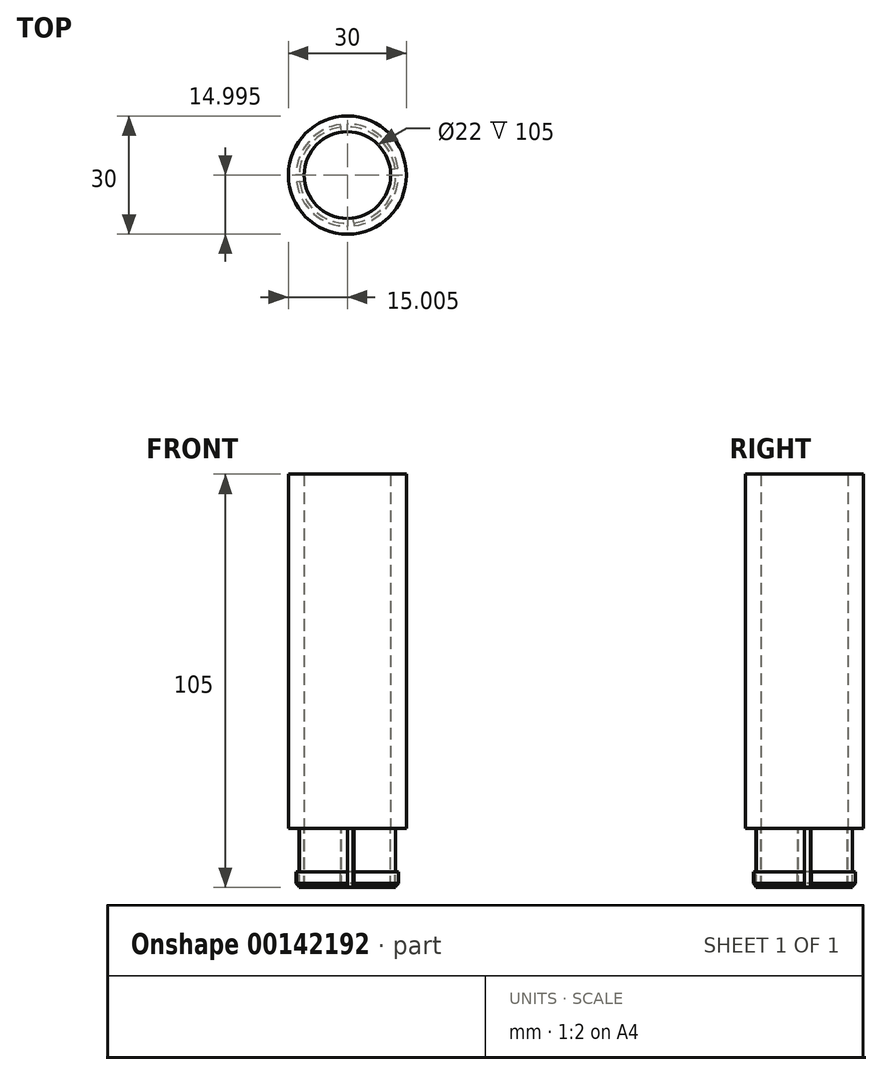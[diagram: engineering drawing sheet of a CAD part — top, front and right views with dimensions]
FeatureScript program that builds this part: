
annotation { "Feature Type Name" : "Feature", "Feature Type Description" : "" }
export const myFeature = defineFeature(function(context is Context, id is Id, definition is map)
    precondition{}
    {
        {
            var Q0;
            Q0=qCreatedBy(makeId("Top.planeOp"),FACE);
            var sketch = newSketch(context, id + "F0", { "sketchPlane" : qUnion([Q0])});
            skCircle(sketch, "E0", {"center": v(-39.95, 28.1) * mm, "radius": 15 * mm});
            skCircle(sketch, "E1", {"center": v(-39.95, 28.1) * mm, "radius": 12.25 * mm});
            skCircle(sketch, "E2", {"center": v(-39.95, 28.1) * mm, "radius": 11 * mm});
            skLineSegment(sketch, "E3", {"start": v(-39.95, 17.1) * mm, "end": v(-39.95, 15.86) * mm});
            skLineSegment(sketch, "E4", {"start": v(-39.95, 15.86) * mm, "end": v(-39.95, 17.1) * mm});
            skLineSegment(sketch, "E5", {"start": v(-39.95, 39.1) * mm, "end": v(-39.95, 40.36) * mm});
            skLineSegment(sketch, "E6", {"start": v(-39.95, 40.36) * mm, "end": v(-39.95, 39.1) * mm});
            skLineSegment(sketch, "E7", {"start": v(-28.95, 28.1) * mm, "end": v(-27.7, 28.1) * mm});
            skLineSegment(sketch, "E8", {"start": v(-27.7, 28.1) * mm, "end": v(-28.95, 28.1) * mm});
            skLineSegment(sketch, "E9", {"start": v(-50.95, 28.1) * mm, "end": v(-52.2, 28.1) * mm});
            skLineSegment(sketch, "E10", {"start": v(-52.2, 28.1) * mm, "end": v(-50.95, 28.1) * mm});
            skLineSegment(sketch, "E11", {"start": v(-29.04, 29.57) * mm, "end": v(-27.8, 29.74) * mm});
            skLineSegment(sketch, "E12", {"start": v(-27.8, 29.74) * mm, "end": v(-29.04, 29.57) * mm});
            skLineSegment(sketch, "E13", {"start": v(-52.09, 26.47) * mm, "end": v(-50.85, 26.64) * mm});
            skLineSegment(sketch, "E14", {"start": v(-41.41, 39) * mm, "end": v(-41.58, 40.25) * mm});
            skLineSegment(sketch, "E15", {"start": v(-41.58, 40.25) * mm, "end": v(-41.41, 39) * mm});
            skLineSegment(sketch, "E16", {"start": v(-38.3, 15.96) * mm, "end": v(-38.48, 17.2) * mm});
            skLineSegment(sketch, "E17.trimOffspring", {"start": v(-38.48, 17.2) * mm, "end": v(-38.3, 15.96) * mm});
            skLineSegment(sketch, "E18.trimOffspring", {"start": v(-50.85, 26.64) * mm, "end": v(-52.09, 26.47) * mm});
            skCircle(sketch, "E19", {"center": v(-39.95, 28.1) * mm, "radius": 13 * mm});
            skLineSegment(sketch, "E20", {"start": v(-50.95, 28.1) * mm, "end": v(-52.95, 28.1) * mm});
            skLineSegment(sketch, "E21", {"start": v(-50.85, 26.64) * mm, "end": v(-52.83, 26.37) * mm});
            skLineSegment(sketch, "E22", {"start": v(-41.41, 39) * mm, "end": v(-41.68, 40.99) * mm});
            skLineSegment(sketch, "E23", {"start": v(-39.95, 39.1) * mm, "end": v(-39.95, 41.1) * mm});
            skLineSegment(sketch, "E24", {"start": v(-29.04, 29.57) * mm, "end": v(-27.06, 29.84) * mm});
            skLineSegment(sketch, "E25", {"start": v(-28.95, 28.1) * mm, "end": v(-26.95, 28.1) * mm});
            skLineSegment(sketch, "E26", {"start": v(-39.95, 17.1) * mm, "end": v(-39.95, 15.1) * mm});
            skLineSegment(sketch, "E27", {"start": v(-38.48, 17.2) * mm, "end": v(-38.2, 15.22) * mm});
            skSolve(sketch);
        }
        {
            var Q0;
            Q0 = qSketchRegion(id + "F0", true);
            var Q1;
            {var subQ0=sQuery(id+"F0.wireOp",EDGE,"E4");Q1=makeQuery(id+"F0.imprint","IMPRINT",FACE,{"disambiguationData":[TD([[makeQuery(id+"F0.imprint","IMPRINT",EDGE,{"derivedFrom":subQ0}),1.0]])]});}
            var Q2;
            Q2=makeQuery(id+"F0.imprint","IMPRINT",FACE,{"disambiguationData":[TD([[makeQuery(id+"F0.imprint","IMPRINT",EDGE,{"derivedFrom":sQuery(id+"F0.wireOp",EDGE,"E19")}),1.0]])]});
            var Q3;
            {var subQ0=sQuery(id+"F0.wireOp",EDGE,"E8");Q3=makeQuery(id+"F0.imprint","IMPRINT",FACE,{"disambiguationData":[TD([[makeQuery(id+"F0.imprint","IMPRINT",EDGE,{"derivedFrom":subQ0}),1.0]])]});}
            var Q4;
            {var subQ0=sQuery(id+"F0.wireOp",EDGE,"E6");Q4=makeQuery(id+"F0.imprint","IMPRINT",FACE,{"disambiguationData":[TD([[makeQuery(id+"F0.imprint","IMPRINT",EDGE,{"derivedFrom":subQ0}),1.0]])]});}
            var Q5;
            {var subQ0=sQuery(id+"F0.wireOp",EDGE,"E10");Q5=makeQuery(id+"F0.imprint","IMPRINT",FACE,{"disambiguationData":[TD([[makeQuery(id+"F0.imprint","IMPRINT",EDGE,{"derivedFrom":subQ0}),1.0]])]});}
            var Q6;
            {var subQ0=sQuery(id+"F0.wireOp",EDGE,"E6");Q6=makeQuery(id+"F0.imprint","IMPRINT",FACE,{"disambiguationData":[TD([[makeQuery(id+"F0.imprint","IMPRINT",EDGE,{"derivedFrom":subQ0}),-1.0]])]});}
            var Q7;
            {var subQ0=sQuery(id+"F0.wireOp",EDGE,"E8");Q7=makeQuery(id+"F0.imprint","IMPRINT",FACE,{"disambiguationData":[TD([[makeQuery(id+"F0.imprint","IMPRINT",EDGE,{"derivedFrom":subQ0}),-1.0]])]});}
            var Q8;
            {var subQ0=sQuery(id+"F0.wireOp",EDGE,"E4");Q8=makeQuery(id+"F0.imprint","IMPRINT",FACE,{"disambiguationData":[TD([[makeQuery(id+"F0.imprint","IMPRINT",EDGE,{"derivedFrom":subQ0}),-1.0]])]});}
            var Q9;
            {var subQ0=sQuery(id+"F0.wireOp",EDGE,"E10");Q9=makeQuery(id+"F0.imprint","IMPRINT",FACE,{"disambiguationData":[TD([[makeQuery(id+"F0.imprint","IMPRINT",EDGE,{"derivedFrom":subQ0}),-1.0]])]});}
            var Q10;
            {var subQ0=sQuery(id+"F0.wireOp",EDGE,"E22");var subQ1=sQuery(id+"F0.wireOp",EDGE,"E1");var subQ2=makeQuery(id+"F0.imprint","INTERSECT",VERTEX,{"derivedFrom":[subQ1,subQ0]});Q10=makeQuery(id+"F0.imprint","IMPRINT",FACE,{"disambiguationData":[TD([[makeQuery(id+"F0.imprint","IMPRINT",EDGE,{"disambiguationData":[TD([[subQ2,-1.0]])],"derivedFrom":subQ1}),1.0]])]});}
            var Q11;
            {var subQ0=sQuery(id+"F0.wireOp",EDGE,"E23");var subQ1=sQuery(id+"F0.wireOp",EDGE,"E1");var subQ2=makeQuery(id+"F0.imprint","INTERSECT",VERTEX,{"derivedFrom":[subQ1,subQ0]});Q11=makeQuery(id+"F0.imprint","IMPRINT",FACE,{"disambiguationData":[TD([[makeQuery(id+"F0.imprint","IMPRINT",EDGE,{"disambiguationData":[TD([[subQ2,-1.0]])],"derivedFrom":subQ1}),1.0]])]});}
            var Q12;
            {var subQ0=sQuery(id+"F0.wireOp",EDGE,"E24");var subQ1=sQuery(id+"F0.wireOp",EDGE,"E1");var subQ2=makeQuery(id+"F0.imprint","INTERSECT",VERTEX,{"derivedFrom":[subQ1,subQ0]});Q12=makeQuery(id+"F0.imprint","IMPRINT",FACE,{"disambiguationData":[TD([[makeQuery(id+"F0.imprint","IMPRINT",EDGE,{"disambiguationData":[TD([[subQ2,-1.0]])],"derivedFrom":subQ1}),1.0]])]});}
            var Q13;
            {var subQ0=sQuery(id+"F0.wireOp",EDGE,"E24");var subQ1=sQuery(id+"F0.wireOp",EDGE,"E1");var subQ2=makeQuery(id+"F0.imprint","INTERSECT",VERTEX,{"derivedFrom":[subQ1,subQ0]});Q13=makeQuery(id+"F0.imprint","IMPRINT",FACE,{"disambiguationData":[TD([[makeQuery(id+"F0.imprint","IMPRINT",EDGE,{"disambiguationData":[TD([[subQ2,1.0]])],"derivedFrom":subQ1}),1.0]])]});}
            var Q14;
            {var subQ0=sQuery(id+"F0.wireOp",EDGE,"E25");var subQ1=sQuery(id+"F0.wireOp",EDGE,"E1");var subQ2=makeQuery(id+"F0.imprint","INTERSECT",VERTEX,{"derivedFrom":[subQ1,subQ0]});Q14=makeQuery(id+"F0.imprint","IMPRINT",FACE,{"disambiguationData":[TD([[makeQuery(id+"F0.imprint","IMPRINT",EDGE,{"disambiguationData":[TD([[subQ2,1.0]])],"derivedFrom":subQ1}),1.0]])]});}
            var Q15;
            {var subQ0=sQuery(id+"F0.wireOp",EDGE,"E26");var subQ1=sQuery(id+"F0.wireOp",EDGE,"E1");var subQ2=makeQuery(id+"F0.imprint","INTERSECT",VERTEX,{"derivedFrom":[subQ1,subQ0]});Q15=makeQuery(id+"F0.imprint","IMPRINT",FACE,{"disambiguationData":[TD([[makeQuery(id+"F0.imprint","IMPRINT",EDGE,{"disambiguationData":[TD([[subQ2,-1.0]])],"derivedFrom":subQ1}),1.0]])]});}
            var Q16;
            {var subQ0=sQuery(id+"F0.wireOp",EDGE,"E21");var subQ1=sQuery(id+"F0.wireOp",EDGE,"E1");var subQ2=makeQuery(id+"F0.imprint","INTERSECT",VERTEX,{"derivedFrom":[subQ1,subQ0]});Q16=makeQuery(id+"F0.imprint","IMPRINT",FACE,{"disambiguationData":[TD([[makeQuery(id+"F0.imprint","IMPRINT",EDGE,{"disambiguationData":[TD([[subQ2,-1.0]])],"derivedFrom":subQ1}),1.0]])]});}
            var Q17;
            {var subQ0=sQuery(id+"F0.wireOp",EDGE,"E20");var subQ1=sQuery(id+"F0.wireOp",EDGE,"E1");var subQ2=makeQuery(id+"F0.imprint","INTERSECT",VERTEX,{"derivedFrom":[subQ1,subQ0]});Q17=makeQuery(id+"F0.imprint","IMPRINT",FACE,{"disambiguationData":[TD([[makeQuery(id+"F0.imprint","IMPRINT",EDGE,{"disambiguationData":[TD([[subQ2,-1.0]])],"derivedFrom":subQ1}),1.0]])]});}
            extrude(context, id + "F1", {"entities" : qUnion([Q0, Q1, Q2, Q3, Q4, Q5, Q6, Q7, Q8, Q9, Q10, Q11, Q12, Q13, Q14, Q15, Q16, Q17]), "depth" : 90 * mm});
        }
        {
            var Q0;
            {var subQ0=sQuery(id+"F0.wireOp",EDGE,"E22");var subQ1=sQuery(id+"F0.wireOp",EDGE,"E1");var subQ2=makeQuery(id+"F0.imprint","INTERSECT",VERTEX,{"derivedFrom":[subQ1,subQ0]});Q0=makeQuery(id+"F0.imprint","IMPRINT",FACE,{"disambiguationData":[TD([[makeQuery(id+"F0.imprint","IMPRINT",EDGE,{"disambiguationData":[TD([[subQ2,-1.0]])],"derivedFrom":subQ1}),1.0]])]});}
            var Q1;
            {var subQ0=sQuery(id+"F0.wireOp",EDGE,"E24");var subQ1=sQuery(id+"F0.wireOp",EDGE,"E1");var subQ2=makeQuery(id+"F0.imprint","INTERSECT",VERTEX,{"derivedFrom":[subQ1,subQ0]});Q1=makeQuery(id+"F0.imprint","IMPRINT",FACE,{"disambiguationData":[TD([[makeQuery(id+"F0.imprint","IMPRINT",EDGE,{"disambiguationData":[TD([[subQ2,-1.0]])],"derivedFrom":subQ1}),1.0]])]});}
            var Q2;
            {var subQ0=sQuery(id+"F0.wireOp",EDGE,"E25");var subQ1=sQuery(id+"F0.wireOp",EDGE,"E1");var subQ2=makeQuery(id+"F0.imprint","INTERSECT",VERTEX,{"derivedFrom":[subQ1,subQ0]});Q2=makeQuery(id+"F0.imprint","IMPRINT",FACE,{"disambiguationData":[TD([[makeQuery(id+"F0.imprint","IMPRINT",EDGE,{"disambiguationData":[TD([[subQ2,1.0]])],"derivedFrom":subQ1}),1.0]])]});}
            var Q3;
            {var subQ0=sQuery(id+"F0.wireOp",EDGE,"E21");var subQ1=sQuery(id+"F0.wireOp",EDGE,"E1");var subQ2=makeQuery(id+"F0.imprint","INTERSECT",VERTEX,{"derivedFrom":[subQ1,subQ0]});Q3=makeQuery(id+"F0.imprint","IMPRINT",FACE,{"disambiguationData":[TD([[makeQuery(id+"F0.imprint","IMPRINT",EDGE,{"disambiguationData":[TD([[subQ2,-1.0]])],"derivedFrom":subQ1}),1.0]])]});}
            extrude(context, id + "F2", {"entities" : qUnion([Q0, Q1, Q2, Q3]), "operationType" : NewBodyOperationType.ADD, "oppositeDirection" : true, "depth" : 15 * mm});
        }
        {
            var Q0;
            {var subQ0=sQuery(id+"F0.wireOp",EDGE,"E24");var subQ1=sQuery(id+"F0.wireOp",EDGE,"E1");var subQ2=makeQuery(id+"F0.imprint","INTERSECT",VERTEX,{"derivedFrom":[subQ1,subQ0]});Q0=makeQuery(id+"F0.imprint","IMPRINT",FACE,{"disambiguationData":[TD([[makeQuery(id+"F0.imprint","IMPRINT",EDGE,{"disambiguationData":[TD([[subQ2,-1.0]])],"derivedFrom":subQ1}),-1.0]])]});}
            var Q1;
            {var subQ0=sQuery(id+"F0.wireOp",EDGE,"E21");var subQ1=sQuery(id+"F0.wireOp",EDGE,"E1");var subQ2=makeQuery(id+"F0.imprint","INTERSECT",VERTEX,{"derivedFrom":[subQ1,subQ0]});Q1=makeQuery(id+"F0.imprint","IMPRINT",FACE,{"disambiguationData":[TD([[makeQuery(id+"F0.imprint","IMPRINT",EDGE,{"disambiguationData":[TD([[subQ2,-1.0]])],"derivedFrom":subQ1}),-1.0]])]});}
            var Q2;
            {var subQ0=sQuery(id+"F0.wireOp",EDGE,"E25");var subQ1=sQuery(id+"F0.wireOp",EDGE,"E1");var subQ2=makeQuery(id+"F0.imprint","INTERSECT",VERTEX,{"derivedFrom":[subQ1,subQ0]});Q2=makeQuery(id+"F0.imprint","IMPRINT",FACE,{"disambiguationData":[TD([[makeQuery(id+"F0.imprint","IMPRINT",EDGE,{"disambiguationData":[TD([[subQ2,1.0]])],"derivedFrom":subQ1}),-1.0]])]});}
            var Q3;
            {var subQ0=sQuery(id+"F0.wireOp",EDGE,"E22");var subQ1=sQuery(id+"F0.wireOp",EDGE,"E1");var subQ2=makeQuery(id+"F0.imprint","INTERSECT",VERTEX,{"derivedFrom":[subQ1,subQ0]});Q3=makeQuery(id+"F0.imprint","IMPRINT",FACE,{"disambiguationData":[TD([[makeQuery(id+"F0.imprint","IMPRINT",EDGE,{"disambiguationData":[TD([[subQ2,-1.0]])],"derivedFrom":subQ1}),-1.0]])]});}
            var Q4;
            Q4=makeQuery(id+"F2.opExtrude","CAP_FACE",FACE,{"disambiguationData":[OSD([sQuery(id+"F0.wireOp",EDGE,"E1"),sQuery(id+"F0.wireOp",EDGE,"E2"),sQuery(id+"F0.wireOp",EDGE,"E25"),sQuery(id+"F0.wireOp",EDGE,"E27")])],"isStart":false});
            extrude(context, id + "F3", {"entities" : qUnion([Q0, Q1, Q2, Q3]), "endBound" : BoundingType.UP_TO_SURFACE, "oppositeDirection" : true, "endBoundEntityFace" : qUnion([Q4]), "depth" : 25 * mm, "hasSecondDirection" : true, "secondDirectionOppositeDirection" : true, "secondDirectionDepth" : 11 * mm});
        }
        {
            var Q0;
            {var subQ0=sQuery(id+"F0.wireOp",EDGE,"E19");Q0=makeQuery(id+"F3.opExtrude","CAP_EDGE",EDGE,{"disambiguationData":[OSD([subQ0]),TDD([makeQuery(id+"F0.imprint","IMPRINT",EDGE,{"disambiguationData":[TD([[makeQuery(id+"F0.imprint","INTERSECT",VERTEX,{"derivedFrom":[subQ0,sQuery(id+"F0.wireOp",EDGE,"E25")]}),1.0]])],"derivedFrom":subQ0})])],"isStart":false});}
            var Q1;
            {var subQ0=sQuery(id+"F0.wireOp",EDGE,"E19");Q1=makeQuery(id+"F3.opExtrude","CAP_EDGE",EDGE,{"disambiguationData":[OSD([subQ0]),TDD([makeQuery(id+"F0.imprint","IMPRINT",EDGE,{"disambiguationData":[TD([[makeQuery(id+"F0.imprint","INTERSECT",VERTEX,{"derivedFrom":[subQ0,sQuery(id+"F0.wireOp",EDGE,"E20")]}),1.0]])],"derivedFrom":subQ0})])],"isStart":false});}
            var Q2;
            {var subQ0=sQuery(id+"F0.wireOp",EDGE,"E19");Q2=makeQuery(id+"F3.opExtrude","CAP_EDGE",EDGE,{"disambiguationData":[OSD([subQ0]),TDD([makeQuery(id+"F0.imprint","IMPRINT",EDGE,{"disambiguationData":[TD([[makeQuery(id+"F0.imprint","INTERSECT",VERTEX,{"derivedFrom":[subQ0,sQuery(id+"F0.wireOp",EDGE,"E21")]}),-1.0]])],"derivedFrom":subQ0})])],"isStart":false});}
            var Q3;
            {var subQ0=sQuery(id+"F0.wireOp",EDGE,"E19");Q3=makeQuery(id+"F3.opExtrude","CAP_EDGE",EDGE,{"disambiguationData":[OSD([subQ0]),TDD([makeQuery(id+"F0.imprint","IMPRINT",EDGE,{"disambiguationData":[TD([[makeQuery(id+"F0.imprint","INTERSECT",VERTEX,{"derivedFrom":[subQ0,sQuery(id+"F0.wireOp",EDGE,"E23")]}),1.0]])],"derivedFrom":subQ0})])],"isStart":false});}
            chamfer(context, id + "F4", {"entities" : qUnion([Q0, Q1, Q2, Q3]), "width" : 1 * mm, "tangentPropagation" : true});
        }
    });
